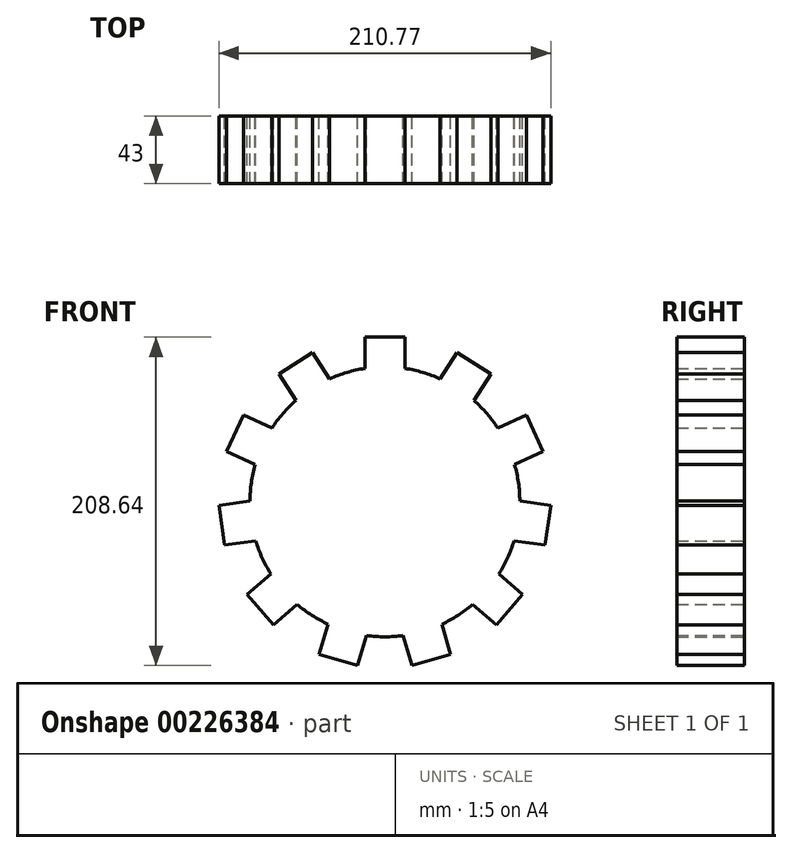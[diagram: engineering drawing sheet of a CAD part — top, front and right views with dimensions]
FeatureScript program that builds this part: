
annotation { "Feature Type Name" : "Feature", "Feature Type Description" : "" }
export const myFeature = defineFeature(function(context is Context, id is Id, definition is map)
    precondition{}
    {
        {
            var Q0;
            Q0=qCreatedBy(makeId("Front.planeOp"),FACE);
            var sketch = newSketch(context, id + "F0", { "sketchPlane" : qUnion([Q0])});
            skArc(sketch, "E0", {"start": v(-136.13, 110.9) * mm, "mid": v(-144.35, 102.62) * mm, "end": v(-151.37, 93.3) * mm});
            skLineSegment(sketch, "E1", {"start": v(-92.34, 131.24) * mm, "end": v(-92.34, 151.14) * mm});
            skLineSegment(sketch, "E2", {"start": v(-66.83, 131.24) * mm, "end": v(-66.83, 151.14) * mm});
            skLineSegment(sketch, "E3", {"start": v(-92.34, 151.14) * mm, "end": v(-66.83, 151.14) * mm});
            skLineSegment(sketch, "E4.1.0", {"start": v(-136.13, 110.9) * mm, "end": v(-146.89, 127.63) * mm});
            skLineSegment(sketch, "E4.1.1", {"start": v(-146.89, 127.63) * mm, "end": v(-125.43, 141.42) * mm});
            skLineSegment(sketch, "E4.1.2", {"start": v(-114.67, 124.68) * mm, "end": v(-125.43, 141.42) * mm});
            skLineSegment(sketch, "E4.2.0", {"start": v(-161.97, 70.1) * mm, "end": v(-180.07, 78.36) * mm});
            skLineSegment(sketch, "E4.2.1", {"start": v(-180.07, 78.36) * mm, "end": v(-169.47, 101.57) * mm});
            skLineSegment(sketch, "E4.2.2", {"start": v(-151.37, 93.3) * mm, "end": v(-169.47, 101.57) * mm});
            skLineSegment(sketch, "E4.3.0", {"start": v(-161.65, 21.81) * mm, "end": v(-181.34, 18.98) * mm});
            skLineSegment(sketch, "E4.3.1", {"start": v(-181.34, 18.98) * mm, "end": v(-184.97, 44.23) * mm});
            skLineSegment(sketch, "E4.3.2", {"start": v(-165.28, 47.06) * mm, "end": v(-184.97, 44.23) * mm});
            skLineSegment(sketch, "E4.4.0", {"start": v(-135.28, -18.64) * mm, "end": v(-150.31, -31.66) * mm});
            skLineSegment(sketch, "E4.4.1", {"start": v(-150.31, -31.66) * mm, "end": v(-167.02, -12.39) * mm});
            skLineSegment(sketch, "E4.4.2", {"start": v(-151.98, 0.64) * mm, "end": v(-167.02, -12.39) * mm});
            skLineSegment(sketch, "E4.5.0", {"start": v(-91.22, -38.4) * mm, "end": v(-96.83, -57.5) * mm});
            skLineSegment(sketch, "E4.5.1", {"start": v(-96.83, -57.5) * mm, "end": v(-121.3, -50.3) * mm});
            skLineSegment(sketch, "E4.5.2", {"start": v(-115.7, -31.22) * mm, "end": v(-121.3, -50.3) * mm});
            skLineSegment(sketch, "E4.6.0", {"start": v(-43.47, -31.22) * mm, "end": v(-37.87, -50.3) * mm});
            skLineSegment(sketch, "E4.6.1", {"start": v(-37.87, -50.3) * mm, "end": v(-62.34, -57.5) * mm});
            skLineSegment(sketch, "E4.6.2", {"start": v(-67.95, -38.4) * mm, "end": v(-62.34, -57.5) * mm});
            skLineSegment(sketch, "E4.7.0", {"start": v(-7.2, 0.64) * mm, "end": v(7.85, -12.39) * mm});
            skLineSegment(sketch, "E4.7.1", {"start": v(7.85, -12.39) * mm, "end": v(-8.86, -31.66) * mm});
            skLineSegment(sketch, "E4.7.2", {"start": v(-23.9, -18.64) * mm, "end": v(-8.86, -31.66) * mm});
            skLineSegment(sketch, "E4.8.0", {"start": v(6.1, 47.06) * mm, "end": v(25.8, 44.23) * mm});
            skLineSegment(sketch, "E4.8.1", {"start": v(25.8, 44.23) * mm, "end": v(22.17, 18.98) * mm});
            skLineSegment(sketch, "E4.8.2", {"start": v(2.48, 21.81) * mm, "end": v(22.17, 18.98) * mm});
            skLineSegment(sketch, "E4.9.0", {"start": v(-7.8, 93.3) * mm, "end": v(10.3, 101.57) * mm});
            skLineSegment(sketch, "E4.9.1", {"start": v(10.3, 101.57) * mm, "end": v(20.9, 78.36) * mm});
            skLineSegment(sketch, "E4.9.2", {"start": v(2.8, 70.1) * mm, "end": v(20.9, 78.36) * mm});
            skLineSegment(sketch, "E4.10.0", {"start": v(-44.5, 124.68) * mm, "end": v(-33.74, 141.42) * mm});
            skLineSegment(sketch, "E4.10.1", {"start": v(-33.74, 141.42) * mm, "end": v(-12.29, 127.63) * mm});
            skLineSegment(sketch, "E4.10.2", {"start": v(-23.04, 110.9) * mm, "end": v(-12.29, 127.63) * mm});
            skArc(sketch, "E5.trimOffspring", {"start": v(-92.34, 131.24) * mm, "mid": v(-103.73, 128.72) * mm, "end": v(-114.67, 124.68) * mm});
            skArc(sketch, "E6.trimOffspring", {"start": v(-44.5, 124.68) * mm, "mid": v(-55.44, 128.72) * mm, "end": v(-66.83, 131.24) * mm});
            skArc(sketch, "E7.trimOffspring", {"start": v(-7.8, 93.3) * mm, "mid": v(-14.82, 102.62) * mm, "end": v(-23.04, 110.9) * mm});
            skArc(sketch, "E8.trimOffspring", {"start": v(6.1, 47.06) * mm, "mid": v(5.24, 58.7) * mm, "end": v(2.8, 70.1) * mm});
            skArc(sketch, "E9.trimOffspring", {"start": v(-7.2, 0.64) * mm, "mid": v(-1.63, 10.9) * mm, "end": v(2.48, 21.81) * mm});
            skArc(sketch, "E10.trimOffspring", {"start": v(-43.47, -31.22) * mm, "mid": v(-33.26, -25.6) * mm, "end": v(-23.9, -18.64) * mm});
            skArc(sketch, "E11.trimOffspring", {"start": v(-91.22, -38.4) * mm, "mid": v(-79.59, -39.2) * mm, "end": v(-67.95, -38.4) * mm});
            skArc(sketch, "E12.trimOffspring", {"start": v(-135.28, -18.64) * mm, "mid": v(-125.92, -25.6) * mm, "end": v(-115.7, -31.22) * mm});
            skArc(sketch, "E13.trimOffspring", {"start": v(-161.65, 21.81) * mm, "mid": v(-157.54, 10.9) * mm, "end": v(-151.98, 0.64) * mm});
            skArc(sketch, "E14.trimOffspring", {"start": v(-161.97, 70.1) * mm, "mid": v(-164.41, 58.7) * mm, "end": v(-165.28, 47.06) * mm});
            skSolve(sketch);
        }
        {
            var Q0;
            Q0=makeQuery(id+"F0.imprint","IMPRINT",FACE,{"disambiguationData":[TD([[makeQuery(id+"F0.imprint","IMPRINT",EDGE,{"derivedFrom":sQuery(id+"F0.wireOp",EDGE,"E0")}),1.0]])]});
            extrude(context, id + "F1", {"entities" : qUnion([Q0]), "depth" : 43 * mm});
        }
    });
